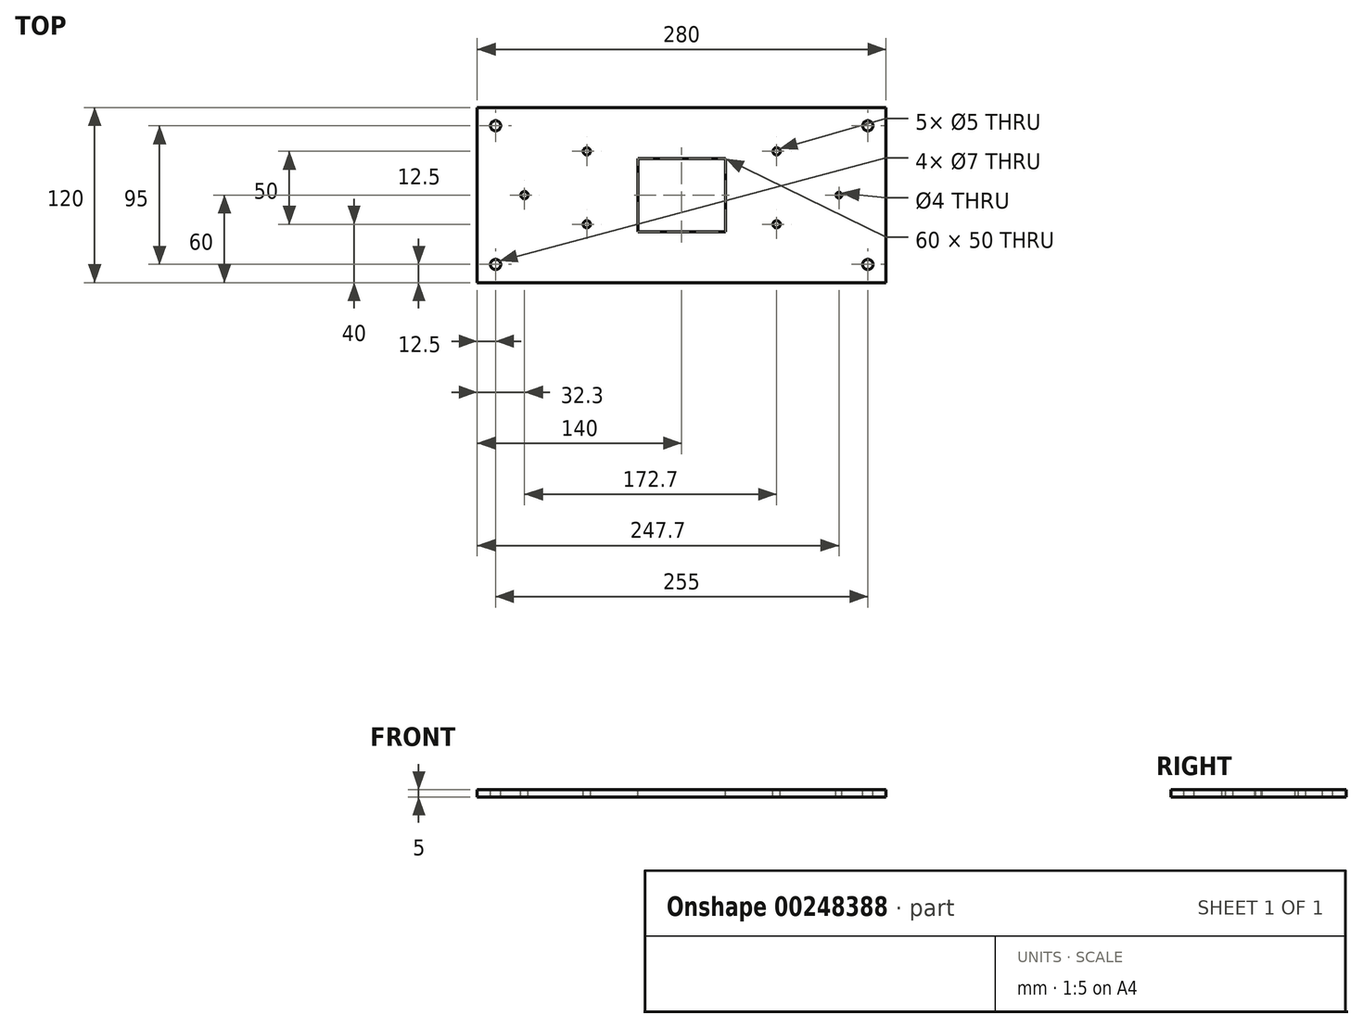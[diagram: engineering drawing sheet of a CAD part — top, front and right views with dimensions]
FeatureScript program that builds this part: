
annotation { "Feature Type Name" : "Feature", "Feature Type Description" : "" }
export const myFeature = defineFeature(function(context is Context, id is Id, definition is map)
    precondition{}
    {
        {
            var Q0;
            Q0=qCreatedBy(makeId("Top.planeOp"),FACE);
            var sketch = newSketch(context, id + "F0", { "sketchPlane" : qUnion([Q0])});
            skLineSegment(sketch, "E0", {"start": v(-140, 60) * mm, "end": v(140, 60) * mm});
            skLineSegment(sketch, "E1", {"start": v(140, 60) * mm, "end": v(140, -60) * mm});
            skLineSegment(sketch, "E2", {"start": v(140, -60) * mm, "end": v(-140, -60) * mm});
            skLineSegment(sketch, "E3", {"start": v(-140, -60) * mm, "end": v(-140, 60) * mm});
            skLineSegment(sketch, "E4", {"start": v(-140, 0) * mm, "end": v(140, 0) * mm, "construction": true});
            skLineSegment(sketch, "E5", {"start": v(0, 60) * mm, "end": v(0, -60) * mm, "construction": true});
            skLineSegment(sketch, "E6.bottom", {"start": v(-30, 25) * mm, "end": v(30, 25) * mm});
            skLineSegment(sketch, "E6.top", {"start": v(-30, -25) * mm, "end": v(30, -25) * mm});
            skLineSegment(sketch, "E6.left", {"start": v(-30, 25) * mm, "end": v(-30, -25) * mm});
            skLineSegment(sketch, "E6.right", {"start": v(30, 25) * mm, "end": v(30, -25) * mm});
            skCircle(sketch, "E7", {"center": v(-127.5, 47.5) * mm, "radius": 3.5 * mm});
            skCircle(sketch, "E8.MirrorC", {"center": v(-127.5, -47.5) * mm, "radius": 3.5 * mm});
            skCircle(sketch, "E9.MirrorC", {"center": v(127.5, -47.5) * mm, "radius": 3.5 * mm});
            skCircle(sketch, "E10.MirrorC", {"center": v(127.5, 47.5) * mm, "radius": 3.5 * mm});
            skCircle(sketch, "E11", {"center": v(-107.7, 0) * mm, "radius": 2.5 * mm});
            skCircle(sketch, "E12", {"center": v(-65, 30) * mm, "radius": 2.5 * mm});
            skCircle(sketch, "E13", {"center": v(-65, -20) * mm, "radius": 2.5 * mm});
            skCircle(sketch, "E14", {"center": v(65, 30) * mm, "radius": 2.5 * mm});
            skCircle(sketch, "E15", {"center": v(65, -20) * mm, "radius": 2.5 * mm});
            skCircle(sketch, "E16", {"center": v(107.7, 0) * mm, "radius": 2 * mm});
            skSolve(sketch);
        }
        {
            var Q0;
            Q0=makeQuery(id+"F0.imprint","IMPRINT",FACE,{"disambiguationData":[TD([[makeQuery(id+"F0.imprint","IMPRINT",EDGE,{"derivedFrom":sQuery(id+"F0.wireOp",EDGE,"E0")}),-1.0]])]});
            extrude(context, id + "F1", {"entities" : qUnion([Q0]), "oppositeDirection" : true, "depth" : 5 * mm});
        }
    });
